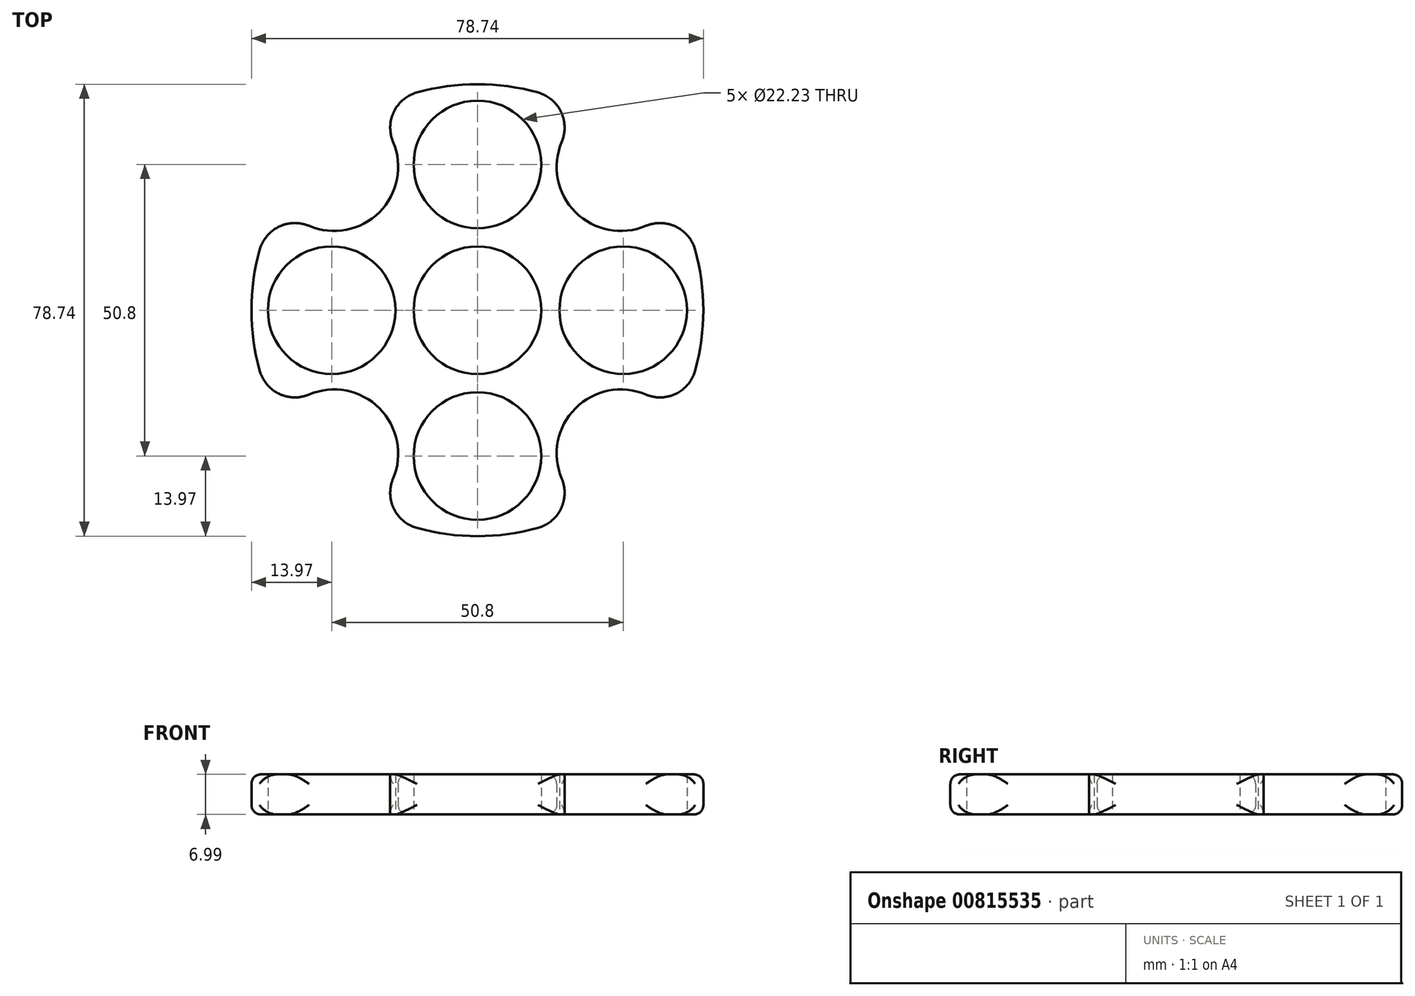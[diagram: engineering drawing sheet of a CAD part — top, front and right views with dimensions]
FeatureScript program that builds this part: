
annotation { "Feature Type Name" : "Feature", "Feature Type Description" : "" }
export const myFeature = defineFeature(function(context is Context, id is Id, definition is map)
    precondition{}
    {
        {
            var Q0;
            Q0=qCreatedBy(makeId("Top.planeOp"),FACE);
            var sketch = newSketch(context, id + "F0", { "sketchPlane" : qUnion([Q0])});
            skCircle(sketch, "E0", {"center": v(0, 0) * mm, "radius": 11.11 * mm});
            skCircle(sketch, "E1", {"center": v(25.4, 0) * mm, "radius": 11.11 * mm});
            skCircle(sketch, "E2.1.0", {"center": v(0, 25.4) * mm, "radius": 11.11 * mm});
            skCircle(sketch, "E2.2.0", {"center": v(-25.4, 0) * mm, "radius": 11.11 * mm});
            skCircle(sketch, "E2.3.0", {"center": v(0, -25.4) * mm, "radius": 11.11 * mm});
            skArc(sketch, "E3", {"start": v(-37.93, 10.54) * mm, "mid": v(-39.37, 0) * mm, "end": v(-37.93, -10.54) * mm});
            skArc(sketch, "E4", {"start": v(14.7, 29.34) * mm, "mid": v(17.08, 17.08) * mm, "end": v(29.34, 14.7) * mm});
            skArc(sketch, "E5.1.0", {"start": v(-29.34, 14.7) * mm, "mid": v(-17.08, 17.08) * mm, "end": v(-14.7, 29.34) * mm});
            skArc(sketch, "E5.2.0", {"start": v(-14.7, -29.34) * mm, "mid": v(-17.08, -17.08) * mm, "end": v(-29.34, -14.7) * mm});
            skArc(sketch, "E5.3.0", {"start": v(29.34, -14.7) * mm, "mid": v(17.08, -17.08) * mm, "end": v(14.7, -29.34) * mm});
            skArc(sketch, "E6.trimOffspring", {"start": v(10.54, 37.93) * mm, "mid": v(0, 39.37) * mm, "end": v(-10.54, 37.93) * mm});
            skArc(sketch, "E7.trimOffspring", {"start": v(37.93, -10.54) * mm, "mid": v(39.37, 0) * mm, "end": v(37.93, 10.54) * mm});
            skArc(sketch, "E8.trimOffspring", {"start": v(-10.54, -37.93) * mm, "mid": v(0, -39.37) * mm, "end": v(10.54, -37.93) * mm});
            skPoint(sketch, "E9.visualSharp", {"position": v(-34.45, 19.05) * mm});
            skArc(sketch, "E9.filletArc", {"start": v(-29.34, 14.7) * mm, "mid": v(-34.57, 14.56) * mm, "end": v(-37.93, 10.54) * mm});
            skPoint(sketch, "E10.visualSharp", {"position": v(-34.45, -19.05) * mm});
            skArc(sketch, "E10.filletArc", {"start": v(-37.93, -10.54) * mm, "mid": v(-34.57, -14.56) * mm, "end": v(-29.34, -14.7) * mm});
            skPoint(sketch, "E11.visualSharp", {"position": v(-19.05, -34.45) * mm});
            skArc(sketch, "E11.filletArc", {"start": v(-14.7, -29.34) * mm, "mid": v(-14.56, -34.57) * mm, "end": v(-10.54, -37.93) * mm});
            skPoint(sketch, "E12.visualSharp", {"position": v(19.05, -34.45) * mm});
            skArc(sketch, "E12.filletArc", {"start": v(10.54, -37.93) * mm, "mid": v(14.56, -34.57) * mm, "end": v(14.7, -29.34) * mm});
            skPoint(sketch, "E13.visualSharp", {"position": v(34.45, -19.05) * mm});
            skArc(sketch, "E13.filletArc", {"start": v(29.34, -14.7) * mm, "mid": v(34.57, -14.56) * mm, "end": v(37.93, -10.54) * mm});
            skPoint(sketch, "E14.visualSharp", {"position": v(34.45, 19.05) * mm});
            skArc(sketch, "E14.filletArc", {"start": v(37.93, 10.54) * mm, "mid": v(34.57, 14.56) * mm, "end": v(29.34, 14.7) * mm});
            skPoint(sketch, "E15.visualSharp", {"position": v(19.05, 34.45) * mm});
            skArc(sketch, "E15.filletArc", {"start": v(14.7, 29.34) * mm, "mid": v(14.56, 34.57) * mm, "end": v(10.54, 37.93) * mm});
            skPoint(sketch, "E16.visualSharp", {"position": v(-19.05, 34.45) * mm});
            skArc(sketch, "E16.filletArc", {"start": v(-10.54, 37.93) * mm, "mid": v(-14.56, 34.57) * mm, "end": v(-14.7, 29.34) * mm});
            skSolve(sketch);
        }
        {
            var Q0;
            Q0=makeQuery(id+"F0.imprint","IMPRINT",FACE,{"disambiguationData":[TD([[makeQuery(id+"F0.imprint","IMPRINT",EDGE,{"derivedFrom":sQuery(id+"F0.wireOp",EDGE,"E0")}),-1.0]])]});
            extrude(context, id + "F1", {"entities" : qUnion([Q0]), "depth" : 7 * mm, "offsetDistance" : 25.4 * mm});
        }
        {
            var Q0;
            Q0=makeQuery(id+"F1.opExtrude","CAP_EDGE",EDGE,{"disambiguationData":[OSD([sQuery(id+"F0.wireOp",EDGE,"E7.trimOffspring")])],"isStart":false});
            var Q1;
            Q1=makeQuery(id+"F1.opExtrude","CAP_EDGE",EDGE,{"disambiguationData":[OSD([sQuery(id+"F0.wireOp",EDGE,"E7.trimOffspring")])],"isStart":true});
            var Q2;
            Q2=makeQuery(id+"F1.opExtrude","CAP_EDGE",EDGE,{"disambiguationData":[OSD([sQuery(id+"F0.wireOp",EDGE,"E8.trimOffspring")])],"isStart":false});
            var Q3;
            Q3=makeQuery(id+"F1.opExtrude","CAP_EDGE",EDGE,{"disambiguationData":[OSD([sQuery(id+"F0.wireOp",EDGE,"E8.trimOffspring")])],"isStart":true});
            var Q4;
            Q4=makeQuery(id+"F1.opExtrude","CAP_EDGE",EDGE,{"disambiguationData":[OSD([sQuery(id+"F0.wireOp",EDGE,"E3")])],"isStart":false});
            var Q5;
            Q5=makeQuery(id+"F1.opExtrude","CAP_EDGE",EDGE,{"disambiguationData":[OSD([sQuery(id+"F0.wireOp",EDGE,"E3")])],"isStart":true});
            var Q6;
            Q6=makeQuery(id+"F1.opExtrude","CAP_EDGE",EDGE,{"disambiguationData":[OSD([sQuery(id+"F0.wireOp",EDGE,"E6.trimOffspring")])],"isStart":true});
            var Q7;
            Q7=makeQuery(id+"F1.opExtrude","CAP_EDGE",EDGE,{"disambiguationData":[OSD([sQuery(id+"F0.wireOp",EDGE,"E6.trimOffspring")])],"isStart":false});
            var Q8;
            Q8=makeQuery(id+"F1.opExtrude","CAP_EDGE",EDGE,{"disambiguationData":[OSD([sQuery(id+"F0.wireOp",EDGE,"E5.1.0")])],"isStart":false});
            var Q9;
            Q9=makeQuery(id+"F1.opExtrude","CAP_EDGE",EDGE,{"disambiguationData":[OSD([sQuery(id+"F0.wireOp",EDGE,"E5.2.0")])],"isStart":false});
            var Q10;
            Q10=makeQuery(id+"F1.opExtrude","CAP_EDGE",EDGE,{"disambiguationData":[OSD([sQuery(id+"F0.wireOp",EDGE,"E5.2.0")])],"isStart":true});
            var Q11;
            Q11=makeQuery(id+"F1.opExtrude","CAP_EDGE",EDGE,{"disambiguationData":[OSD([sQuery(id+"F0.wireOp",EDGE,"E5.3.0")])],"isStart":true});
            var Q12;
            Q12=makeQuery(id+"F1.opExtrude","CAP_EDGE",EDGE,{"disambiguationData":[OSD([sQuery(id+"F0.wireOp",EDGE,"E5.3.0")])],"isStart":false});
            var Q13;
            Q13=makeQuery(id+"F1.opExtrude","CAP_EDGE",EDGE,{"disambiguationData":[OSD([sQuery(id+"F0.wireOp",EDGE,"E5.1.0")])],"isStart":true});
            var Q14;
            Q14=makeQuery(id+"F1.opExtrude","CAP_EDGE",EDGE,{"disambiguationData":[OSD([sQuery(id+"F0.wireOp",EDGE,"E4")])],"isStart":true});
            var Q15;
            Q15=makeQuery(id+"F1.opExtrude","CAP_EDGE",EDGE,{"disambiguationData":[OSD([sQuery(id+"F0.wireOp",EDGE,"E4")])],"isStart":false});
            fillet(context, id + "F2", {"entities" : qUnion([Q0, Q1, Q2, Q3, Q4, Q5, Q6, Q7, Q8, Q9, Q10, Q11, Q12, Q13, Q14, Q15]), "radius" : 1.65 * mm, "allowEdgeOverflow" : false});
        }
    });
